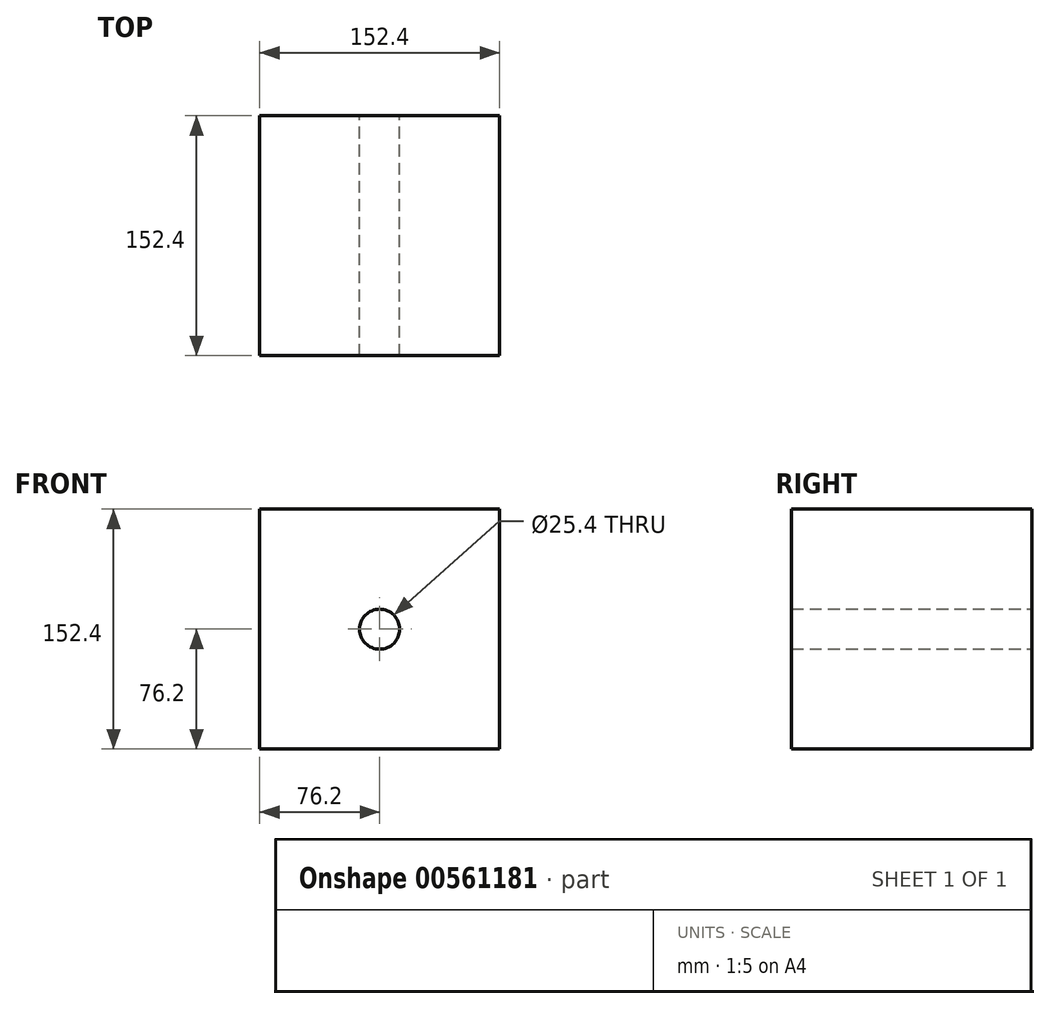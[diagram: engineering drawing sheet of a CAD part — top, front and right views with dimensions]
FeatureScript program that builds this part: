
annotation { "Feature Type Name" : "Feature", "Feature Type Description" : "" }
export const myFeature = defineFeature(function(context is Context, id is Id, definition is map)
    precondition{}
    {
        {
            var Q0;
            Q0=qCreatedBy(makeId("Front.planeOp"),FACE);
            var sketch = newSketch(context, id + "F0", { "sketchPlane" : qUnion([Q0])});
            skLineSegment(sketch, "E0.bottom", {"start": v(-76.2, 76.2) * mm, "end": v(76.2, 76.2) * mm});
            skLineSegment(sketch, "E0.top", {"start": v(-76.2, -76.2) * mm, "end": v(76.2, -76.2) * mm});
            skLineSegment(sketch, "E0.left", {"start": v(-76.2, 76.2) * mm, "end": v(-76.2, -76.2) * mm});
            skLineSegment(sketch, "E0.right", {"start": v(76.2, 76.2) * mm, "end": v(76.2, -76.2) * mm});
            skPoint(sketch, "E0.middle", {"position": v(0, 0) * mm});
            skCircle(sketch, "E1", {"center": v(0, 0) * mm, "radius": 12.7 * mm});
            skSolve(sketch);
        }
        {
            var Q0;
            Q0 = qSketchRegion(id + "F0", true);
            extrude(context, id + "F1", {"entities" : qUnion([Q0]), "depth" : 152.4 * mm, "offsetDistance" : 25.4 * mm});
        }
        {
            var Q0;
            Q0 = qSketchRegion(id + "F0", true);
            extrude(context, id + "F2", {"entities" : qUnion([Q0]), "operationType" : NewBodyOperationType.REMOVE, "oppositeDirection" : true, "depth" : 152.4 * mm, "offsetDistance" : 25.4 * mm});
        }
    });
